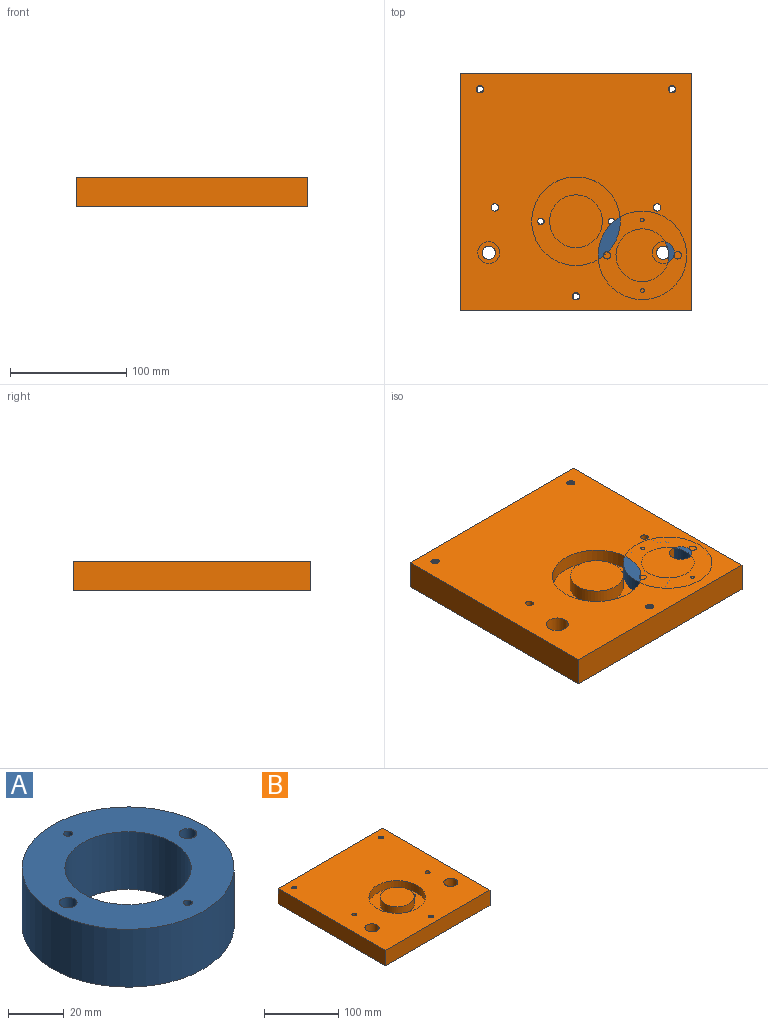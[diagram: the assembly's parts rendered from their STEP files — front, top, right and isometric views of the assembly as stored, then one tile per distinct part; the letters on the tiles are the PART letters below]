
ASSEMBLY  parts=2 mates=1
PART A: 8 faces, bbox 76.2x76.2x25.4 mm
  f0: cylinder r=38.1mm len=76.2mm, axis (0,0,-1), area 6080.5mm2, adj f1,f2
  f1: plane 76.2x76.2mm, normal (0,0,1), area 2863.8mm2, adj f0,f3,f4,f5,f6,f7
  f2: plane 76.2x76.2mm, normal (0,0,-1), area 2863.8mm2, adj f0,f3,f4,f5,f6,f7
  f3: cylinder r=22.69mm len=45.38mm, axis (0,0,1), area 3621.2mm2, adj f1,f2
  f4: cylinder r=1.59mm len=25.4mm, axis (0,0,1), area 253.4mm2, adj f1,f2
  f5: cylinder r=1.59mm len=25.4mm, axis (0,0,1), area 253.4mm2, adj f1,f2
  f6: cylinder r=3.17mm len=25.4mm, axis (0,0,1), area 506.7mm2, adj f1,f2
  f7: cylinder r=3.17mm len=25.4mm, axis (0,0,1), area 506.7mm2, adj f1,f2
PART B: 41 faces, bbox 199.7x204.7x26.2 mm
  f0: cylinder r=2.54mm len=12.7mm, axis (0,0,1), area 51mm2, adj f6,f7,f8,f36
  f1: cylinder r=2.54mm len=12.7mm, axis (0,0,1), area 51mm2, adj f3,f4,f8,f36
  f2: cylinder r=3.11mm len=12.7mm, axis (0,0,-1), area 30.9mm2, adj f3,f4,f8,f36
  f3: bspline ~13.43x6.23mm, area 140.8mm2, adj f1,f2,f8,f36
  f4: bspline ~13.56x6.23mm, area 141.4mm2, adj f1,f2,f8,f36
  f5: cylinder r=3.11mm len=12.7mm, axis (0,0,-1), area 30.9mm2, adj f6,f7,f8,f36
  f6: bspline ~13.43x6.23mm, area 140.8mm2, adj f0,f5,f8,f36
  f7: bspline ~13.56x6.23mm, area 141.4mm2, adj f0,f5,f8,f36
  f8: plane 204.71x199.66mm, normal (0,0,-1), area 40294.6mm2, adj f0,f1,f2,f3,f4,f5,f6,f7
  f9: cylinder r=3.17mm len=25.4mm, axis (0,0,1), area 80.4mm2, adj f8,f16,f32,f33,f34
  f10: cylinder r=3.17mm len=25.4mm, axis (0,0,1), area 80.4mm2, adj f8,f16,f28,f29,f30
  f11: cylinder r=3.17mm len=25.4mm, axis (0,0,1), area 80.4mm2, adj f8,f16,f24,f25,f26
  f12: plane 204.35x25.4mm, normal (-1,0,0), area 5190.5mm2, adj f8,f13,f15,f16
  f13: plane 199.3x25.4mm, normal (0,-1,0), area 5062.2mm2, adj f8,f12,f14,f16
  f14: plane 204.35x25.4mm, normal (1,0,0), area 5190.5mm2, adj f8,f13,f15,f16
  f15: plane 199.3x25.4mm, normal (0,1,0), area 5062.2mm2, adj f8,f12,f14,f16
  f16: plane 204.35x199.3mm, normal (0,0,1), area 35447.3mm2, adj f9,f10,f11,f12,f13,f14,f15,f19
  f17: cylinder r=5.71mm len=12.7mm, axis (0,0,1), area 456mm2, adj f8,f18
  f18: plane 18.9x18.9mm, normal (0,0,1), area 177.9mm2, adj f17,f19
  f19: cylinder r=9.45mm len=18.9mm, axis (0,0,1), area 754mm2, adj f16,f18
  f20: cylinder r=5.71mm len=12.7mm, axis (0,0,1), area 456mm2, adj f8,f21
  f21: plane 18.9x18.9mm, normal (0,0,1), area 177.9mm2, adj f20,f22
  f22: cylinder r=9.45mm len=18.9mm, axis (0,0,1), area 754mm2, adj f16,f21
  f23: cylinder r=3.86mm len=25mm, axis (0,0,-1), area 85.7mm2, adj f8,f24,f25,f26
  f24: bspline ~25.8x7.73mm, area 349mm2, adj f8,f11,f23,f26
  f25: bspline ~25.32x7.73mm, area 341.5mm2, adj f8,f11,f23,f26
  f26: plane 0.95x0.69mm, normal (0,1,0), area 0.4mm2, adj f11,f23,f24,f25
  f27: cylinder r=3.86mm len=25mm, axis (0,0,-1), area 85.7mm2, adj f8,f28,f29,f30
  f28: bspline ~25.8x7.73mm, area 349mm2, adj f8,f10,f27,f30
  f29: bspline ~25.32x7.73mm, area 341.5mm2, adj f8,f10,f27,f30
  f30: plane 0.95x0.69mm, normal (0,1,0), area 0.4mm2, adj f10,f27,f28,f29
  f31: cylinder r=3.86mm len=25mm, axis (0,0,-1), area 85.7mm2, adj f8,f32,f33,f34
  f32: bspline ~25.8x7.73mm, area 349mm2, adj f8,f9,f31,f34
  f33: bspline ~25.32x7.73mm, area 341.5mm2, adj f8,f9,f31,f34
  f34: plane 0.95x0.69mm, normal (0,1,0), area 0.4mm2, adj f9,f31,f32,f33
  f35: cylinder r=38.1mm len=76.2mm, axis (0,0,1), area 3040.2mm2, adj f16,f36
  f36: plane 76.49x76.49mm, normal (0,0,1), area 2893.8mm2, adj f0,f1,f2,f3,f4,f5,f6,f7
  f37: cylinder r=22.69mm len=45.38mm, axis (0,0,1), area 1810.6mm2, adj f36,f38
  f38: plane 45.38x45.38mm, normal (0,0,1), area 1617.4mm2, adj f37
  f39: cylinder r=3.17mm len=25.4mm, axis (0,0,1), area 506.7mm2, adj f8,f16
  f40: cylinder r=3.17mm len=25.4mm, axis (0,0,1), area 506.7mm2, adj f8,f16
PLACE A t=(134.07,9.15,43.37)mm
PLACE B t=(77,63.61,43.37)mm
MATE planar B.f35 <-> A.f0  axis (0,0,1) through (77,38.44,68.77)mm
